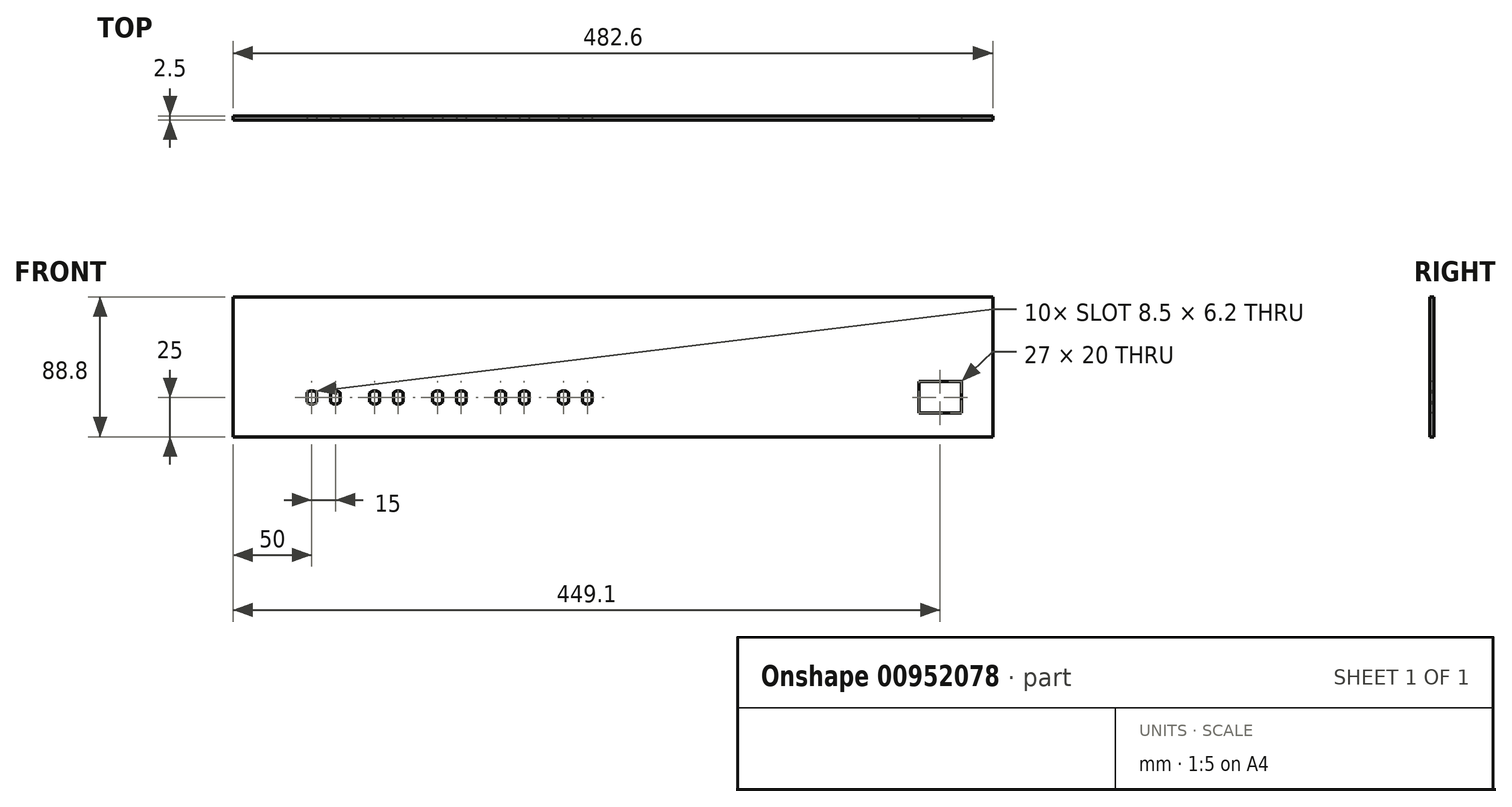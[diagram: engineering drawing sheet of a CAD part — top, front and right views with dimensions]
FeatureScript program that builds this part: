
annotation { "Feature Type Name" : "Feature", "Feature Type Description" : "" }
export const myFeature = defineFeature(function(context is Context, id is Id, definition is map)
    precondition{}
    {
        {
            var Q0;
            Q0=qCreatedBy(makeId("Front.planeOp"),FACE);
            var sketch = newSketch(context, id + "F0", { "sketchPlane" : qUnion([Q0])});
            skLineSegment(sketch, "E0.bottom", {"start": v(0, 0) * mm, "end": v(482.6, 0) * mm});
            skLineSegment(sketch, "E0.top", {"start": v(0, 88.8) * mm, "end": v(482.6, 88.8) * mm});
            skLineSegment(sketch, "E0.left", {"start": v(0, 0) * mm, "end": v(0, 88.8) * mm});
            skLineSegment(sketch, "E0.right", {"start": v(482.6, 0) * mm, "end": v(482.6, 88.8) * mm});
            skSolve(sketch);
        }
        {
            var Q0;
            Q0=makeQuery(id+"F0.imprint","IMPRINT",FACE,{"disambiguationData":[TD([[makeQuery(id+"F0.imprint","IMPRINT",EDGE,{"derivedFrom":sQuery(id+"F0.wireOp",EDGE,"E0.bottom")}),1.0]])]});
            var sketch = newSketch(context, id + "F1", { "sketchPlane" : qUnion([Q0])});
            skLineSegment(sketch, "E1.bottom", {"start": v(435.6, 15) * mm, "end": v(462.6, 15) * mm});
            skLineSegment(sketch, "E1.top", {"start": v(435.6, 35) * mm, "end": v(462.6, 35) * mm});
            skLineSegment(sketch, "E1.left", {"start": v(435.6, 15) * mm, "end": v(435.6, 35) * mm});
            skLineSegment(sketch, "E1.right", {"start": v(462.6, 15) * mm, "end": v(462.6, 35) * mm});
            skArc(sketch, "E2", {"start": v(46.9, 22.1) * mm, "mid": v(50, 20.75) * mm, "end": v(53.1, 22.1) * mm});
            skLineSegment(sketch, "E3", {"start": v(46.9, 27.9) * mm, "end": v(46.9, 22.1) * mm});
            skLineSegment(sketch, "E4", {"start": v(50, 25) * mm, "end": v(50, 29.25) * mm, "construction": true});
            skLineSegment(sketch, "E5.MirrorCS", {"start": v(53.1, 27.9) * mm, "end": v(53.1, 22.1) * mm});
            skArc(sketch, "E6.trimOffspring", {"start": v(53.1, 27.9) * mm, "mid": v(50, 29.25) * mm, "end": v(46.9, 27.9) * mm});
            skArc(sketch, "E7.1.0.0", {"start": v(61.9, 22.1) * mm, "mid": v(65, 20.75) * mm, "end": v(68.1, 22.1) * mm});
            skLineSegment(sketch, "E7.1.0.1", {"start": v(61.9, 27.9) * mm, "end": v(61.9, 22.1) * mm});
            skLineSegment(sketch, "E7.1.0.2", {"start": v(65, 25) * mm, "end": v(65, 29.25) * mm, "construction": true});
            skArc(sketch, "E7.1.0.3", {"start": v(68.1, 27.9) * mm, "mid": v(65, 29.25) * mm, "end": v(61.9, 27.9) * mm});
            skLineSegment(sketch, "E7.1.0.4", {"start": v(68.1, 27.9) * mm, "end": v(68.1, 22.1) * mm});
            skLineSegment(sketch, "E7.direction1", {"start": v(46.9, 22.1) * mm, "end": v(61.9, 22.1) * mm, "construction": true});
            skLineSegment(sketch, "E8.1.0.0", {"start": v(108.1, 27.9) * mm, "end": v(108.1, 22.1) * mm});
            skLineSegment(sketch, "E8.1.0.1", {"start": v(93.1, 27.9) * mm, "end": v(93.1, 22.1) * mm});
            skArc(sketch, "E8.1.0.2", {"start": v(101.9, 22.1) * mm, "mid": v(105, 20.75) * mm, "end": v(108.1, 22.1) * mm});
            skLineSegment(sketch, "E8.1.0.3", {"start": v(90, 25) * mm, "end": v(90, 29.25) * mm, "construction": true});
            skArc(sketch, "E8.1.0.4", {"start": v(93.1, 27.9) * mm, "mid": v(90, 29.25) * mm, "end": v(86.9, 27.9) * mm});
            skLineSegment(sketch, "E8.1.0.5", {"start": v(101.9, 27.9) * mm, "end": v(101.9, 22.1) * mm});
            skArc(sketch, "E8.1.0.6", {"start": v(86.9, 22.1) * mm, "mid": v(90, 20.75) * mm, "end": v(93.1, 22.1) * mm});
            skLineSegment(sketch, "E8.1.0.7", {"start": v(86.9, 22.1) * mm, "end": v(101.9, 22.1) * mm, "construction": true});
            skLineSegment(sketch, "E8.1.0.8", {"start": v(105, 25) * mm, "end": v(105, 29.25) * mm, "construction": true});
            skLineSegment(sketch, "E8.1.0.9", {"start": v(86.9, 27.9) * mm, "end": v(86.9, 22.1) * mm});
            skArc(sketch, "E8.1.0.10", {"start": v(108.1, 27.9) * mm, "mid": v(105, 29.25) * mm, "end": v(101.9, 27.9) * mm});
            skLineSegment(sketch, "E8.2.0.0", {"start": v(148.1, 27.9) * mm, "end": v(148.1, 22.1) * mm});
            skLineSegment(sketch, "E8.2.0.1", {"start": v(133.1, 27.9) * mm, "end": v(133.1, 22.1) * mm});
            skArc(sketch, "E8.2.0.2", {"start": v(141.9, 22.1) * mm, "mid": v(145, 20.75) * mm, "end": v(148.1, 22.1) * mm});
            skLineSegment(sketch, "E8.2.0.3", {"start": v(130, 25) * mm, "end": v(130, 29.25) * mm, "construction": true});
            skArc(sketch, "E8.2.0.4", {"start": v(133.1, 27.9) * mm, "mid": v(130, 29.25) * mm, "end": v(126.9, 27.9) * mm});
            skLineSegment(sketch, "E8.2.0.5", {"start": v(141.9, 27.9) * mm, "end": v(141.9, 22.1) * mm});
            skArc(sketch, "E8.2.0.6", {"start": v(126.9, 22.1) * mm, "mid": v(130, 20.75) * mm, "end": v(133.1, 22.1) * mm});
            skLineSegment(sketch, "E8.2.0.7", {"start": v(126.9, 22.1) * mm, "end": v(141.9, 22.1) * mm, "construction": true});
            skLineSegment(sketch, "E8.2.0.8", {"start": v(145, 25) * mm, "end": v(145, 29.25) * mm, "construction": true});
            skLineSegment(sketch, "E8.2.0.9", {"start": v(126.9, 27.9) * mm, "end": v(126.9, 22.1) * mm});
            skArc(sketch, "E8.2.0.10", {"start": v(148.1, 27.9) * mm, "mid": v(145, 29.25) * mm, "end": v(141.9, 27.9) * mm});
            skLineSegment(sketch, "E8.3.0.0", {"start": v(188.1, 27.9) * mm, "end": v(188.1, 22.1) * mm});
            skLineSegment(sketch, "E8.3.0.1", {"start": v(173.1, 27.9) * mm, "end": v(173.1, 22.1) * mm});
            skArc(sketch, "E8.3.0.2", {"start": v(181.9, 22.1) * mm, "mid": v(185, 20.75) * mm, "end": v(188.1, 22.1) * mm});
            skLineSegment(sketch, "E8.3.0.3", {"start": v(170, 25) * mm, "end": v(170, 29.25) * mm, "construction": true});
            skArc(sketch, "E8.3.0.4", {"start": v(173.1, 27.9) * mm, "mid": v(170, 29.25) * mm, "end": v(166.9, 27.9) * mm});
            skLineSegment(sketch, "E8.3.0.5", {"start": v(181.9, 27.9) * mm, "end": v(181.9, 22.1) * mm});
            skArc(sketch, "E8.3.0.6", {"start": v(166.9, 22.1) * mm, "mid": v(170, 20.75) * mm, "end": v(173.1, 22.1) * mm});
            skLineSegment(sketch, "E8.3.0.7", {"start": v(166.9, 22.1) * mm, "end": v(181.9, 22.1) * mm, "construction": true});
            skLineSegment(sketch, "E8.3.0.8", {"start": v(185, 25) * mm, "end": v(185, 29.25) * mm, "construction": true});
            skLineSegment(sketch, "E8.3.0.9", {"start": v(166.9, 27.9) * mm, "end": v(166.9, 22.1) * mm});
            skArc(sketch, "E8.3.0.10", {"start": v(188.1, 27.9) * mm, "mid": v(185, 29.25) * mm, "end": v(181.9, 27.9) * mm});
            skLineSegment(sketch, "E8.4.0.0", {"start": v(228.1, 27.9) * mm, "end": v(228.1, 22.1) * mm});
            skLineSegment(sketch, "E8.4.0.1", {"start": v(213.1, 27.9) * mm, "end": v(213.1, 22.1) * mm});
            skArc(sketch, "E8.4.0.2", {"start": v(221.9, 22.1) * mm, "mid": v(225, 20.75) * mm, "end": v(228.1, 22.1) * mm});
            skLineSegment(sketch, "E8.4.0.3", {"start": v(210, 25) * mm, "end": v(210, 29.25) * mm, "construction": true});
            skArc(sketch, "E8.4.0.4", {"start": v(213.1, 27.9) * mm, "mid": v(210, 29.25) * mm, "end": v(206.9, 27.9) * mm});
            skLineSegment(sketch, "E8.4.0.5", {"start": v(221.9, 27.9) * mm, "end": v(221.9, 22.1) * mm});
            skArc(sketch, "E8.4.0.6", {"start": v(206.9, 22.1) * mm, "mid": v(210, 20.75) * mm, "end": v(213.1, 22.1) * mm});
            skLineSegment(sketch, "E8.4.0.7", {"start": v(206.9, 22.1) * mm, "end": v(221.9, 22.1) * mm, "construction": true});
            skLineSegment(sketch, "E8.4.0.8", {"start": v(225, 25) * mm, "end": v(225, 29.25) * mm, "construction": true});
            skLineSegment(sketch, "E8.4.0.9", {"start": v(206.9, 27.9) * mm, "end": v(206.9, 22.1) * mm});
            skArc(sketch, "E8.4.0.10", {"start": v(228.1, 27.9) * mm, "mid": v(225, 29.25) * mm, "end": v(221.9, 27.9) * mm});
            skLineSegment(sketch, "E8.direction1", {"start": v(46.9, 22.1) * mm, "end": v(86.9, 22.1) * mm, "construction": true});
            skSolve(sketch);
        }
        {
            var Q0;
            Q0 = qSketchRegion(id + "F0", true);
            extrude(context, id + "F2", {"entities" : qUnion([Q0]), "oppositeDirection" : true, "depth" : 2.5 * mm, "offsetDistance" : 25 * mm});
        }
        {
            var Q0;
            Q0 = qSketchRegion(id + "F1", true);
            extrude(context, id + "F3", {"entities" : qUnion([Q0]), "operationType" : NewBodyOperationType.REMOVE, "endBound" : BoundingType.THROUGH_ALL, "oppositeDirection" : true, "depth" : 25 * mm, "offsetDistance" : 25 * mm});
        }
    });
